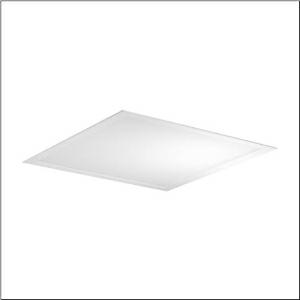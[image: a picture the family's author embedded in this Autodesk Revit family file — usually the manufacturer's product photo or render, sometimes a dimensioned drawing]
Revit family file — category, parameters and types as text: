
# Revit family: apollon_31_square_51mp11wd2442
name_source: partatom
category: Lighting Fixtures
units: mm (PartAtom-declared; Revit-internal decimal feet)

## family parameters
Cut with Voids When Loaded = No
Host = Face
Light Source = No
Part Type = Normal
Room Calculation Point = No
Round Connector Dimension = Use Diameter
Shared = No

## types (1)
- Apollon 31 square (1 x LED, 4000 lm, 27.5 W, 4000K)
    Apparent Load = 28 VA
    CIE Flux Codes = 61 87 97 100 100
    Color Rendering = 80
    Color Temperature = 4000K
    Default Elevation = 1800 mm
    Description = Apollon 31 square, office luminaire, primary optical cover: micro prismatic cover, of PMMA, CAT 2 (L<= 3000cd/m²), light emission: direct distribution, primary light characteristic: symmetric, installation type: lay-in mounting, recessed, LED, rated luminous flux: 4.000lm, luminous efficacy: 145lm/W, light colour: 840, colour temperature: 4000K, control gear: DALI 2, Multilumen, with terminal, 5-pole, mains connection: 220..240V, AC/DC, 0/50..60Hz, rated input power: 28W, suitable for self-contained emergency lighting element 58DB00B013A with integrated self-test function according to EN 60598-2-22, housing, of aluminium, coated, traffic white (RAL 9016), module: M625, length: 620mm, width: 620mm, height: 62mm, housing upper side, of sheet steel, coated, protection rating (complete): IP20, protection rating (lamp compartment, on room side): IP40, insulation class (complete): insulation class II (safety insulation), certification: CE, ENEC, impact resistance: IK03, permissible operating ambient temperature: -20..+40°C, standard: EN 60598-2-22, corresponds to IFS (International Featured Standards) requirements for safety and quality in the food industry, packaging unit: 1 piece
    Height = 0 mm  [stored 0 ft]
    Lamp = 1 x LED
    Lamp Light Flux = 4000 lm
    Lamp Power = 27.5 W
    Lamp count = 1
    Length = 620 mm
    Luminous efficacy = 145 lm/W
    Manufacturer = Siteco
    ModVariant = No
    Model = 51MP11WD2442
    Mounting Place = Ceiling
    Mounting Type = Recessed
    Number of Poles = 1
    OnlyDefault = Yes
    Power Factor = 1
    Product Name = Apollon 31 square
    Product group = office luminaire | ceiling recessed
    ProductGroupID = 400
    Protection Class = Protection class II
    Protection Degree = IP 20
    RLX_Detail_Level = 1
    RLX_Emergency_Light_Flux = 0 lm
    RLX_Emergency_Type = 0
    RLX_Emergency_Type_DB = No
    RlxData = <blob elided: 13297 chars, md5=5195efbc>
    Socket = socket
    Standby Power = 0 W
    System Light Flux = 4000 lm
    System Power = 28 W
    Type Comments = Product without accessories
    Type Image = l_1291039.jpg
    URL = http://relux.com
    VarID = ---
    Voltage = 0 V
    Weight = 0.00 kg
    Width = 620 mm

note: [stored X ft] marks values corroborated as IEEE doubles in the binary element streams (Revit-internal decimal feet)

## geometry (parser evidence)
native form markers: Sweep x10
no freeform markers — native parametric forms only
